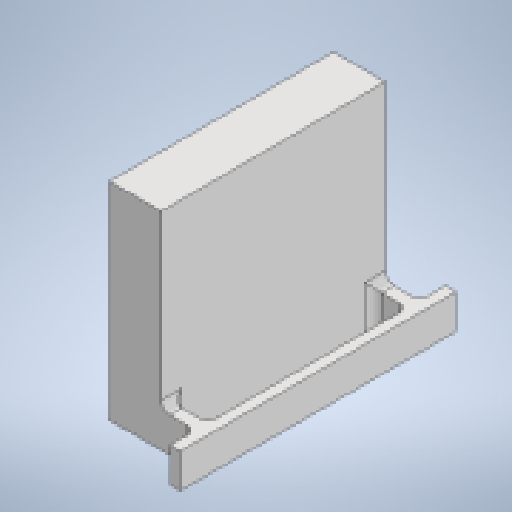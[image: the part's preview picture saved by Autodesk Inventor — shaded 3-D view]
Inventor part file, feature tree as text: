
AUTODESK INVENTOR PART (.ipt)
format: ipt  version: 2024 (Build 280153000, 153)  size: 256,000 bytes
history: native  units: mm
features: extrude x5, sketch x5, fillet x2
ambient origin geometry x8: Origin, YZ Plane, XZ Plane, XY Plane, X Axis, Y Axis, Z Axis, Center Point
bodies: Solid1 (feature_tree)
feature tree (12):
  extrude  "Extrusion1"  Depth=160.0mm
  extrude  "Extrusion2"  Depth=15.0mm
  extrude  "Extrusion3"  Depth=20.0mm
  extrude  "Extrusion4"  Depth=30.0mm
  extrude  "Extrusion5"  Depth=16.0mm
  fillet  "Fillet1"  Radius=50.0mm
  fillet  "Fillet2"  Radius=50.0mm
  sketch  "Sketch1"  dims[d0=6.0mm d1=160.0mm]
  sketch  "Sketch2"  dims[d2=20.0mm d3=0.0mm d4=15.0mm]
  sketch  "Sketch3"  dims[d5=15.0mm d6=20.0mm]
  sketch  "Sketch4"  dims[d7=50.0mm d8=0.0mm d9=30.0mm]
  sketch  "Sketch6"  dims[d10=100.0mm d11=0.0mm d12=16.0mm d13=50.0mm d14=50.0mm d15=0.0mm d16=7.0mm d17=6.0mm d18=7.0mm d19=50.0mm d20=0.0mm d21=5.0mm d22=5.0mm]
